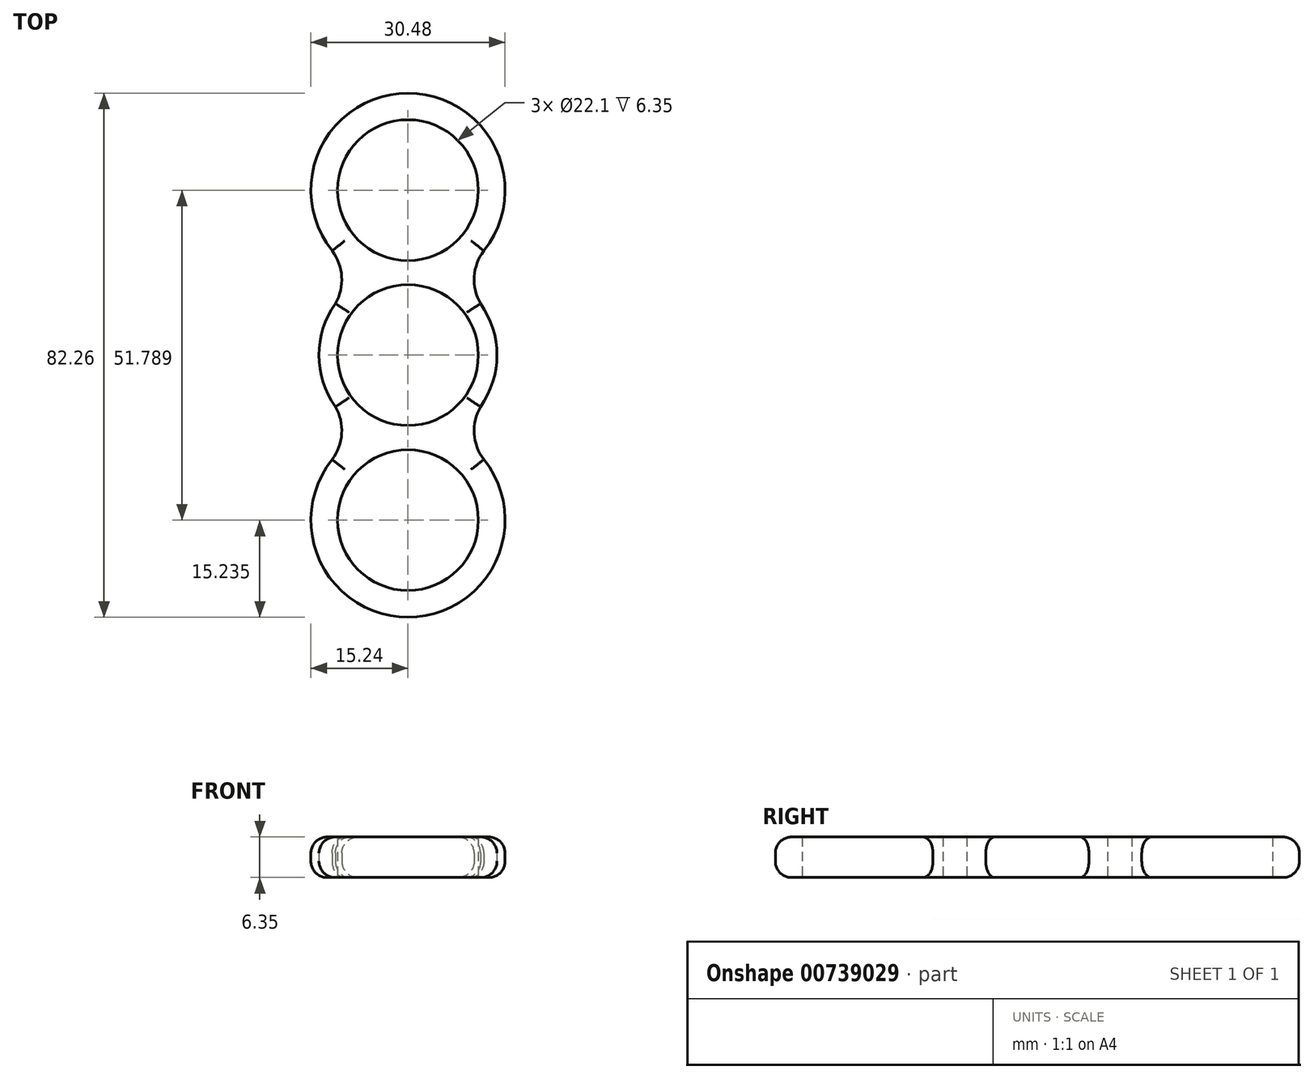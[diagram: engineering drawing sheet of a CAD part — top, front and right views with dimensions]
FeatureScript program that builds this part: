
annotation { "Feature Type Name" : "Feature", "Feature Type Description" : "" }
export const myFeature = defineFeature(function(context is Context, id is Id, definition is map)
    precondition{}
    {
        {
            var Q0;
            Q0=qCreatedBy(makeId("Top.planeOp"),FACE);
            var sketch = newSketch(context, id + "F0", { "sketchPlane" : qUnion([Q0])});
            skArc(sketch, "E0", {"start": v(-11.39, 8.09) * mm, "mid": v(-13.97, 0) * mm, "end": v(-11.39, -8.09) * mm});
            skCircle(sketch, "E1", {"center": v(0, 25.9) * mm, "radius": 11.05 * mm});
            skArc(sketch, "E2", {"start": v(11.9, 16.39) * mm, "mid": v(0, 41.13) * mm, "end": v(-11.9, 16.39) * mm});
            skCircle(sketch, "E3.1.0", {"center": v(0, -25.9) * mm, "radius": 11.05 * mm});
            skArc(sketch, "E3.1.1", {"start": v(-11.9, -16.39) * mm, "mid": v(0, -41.13) * mm, "end": v(11.9, -16.39) * mm});
            skArc(sketch, "E4.trimOffspring", {"start": v(11.39, -8.09) * mm, "mid": v(13.97, 0) * mm, "end": v(11.39, 8.09) * mm});
            skPoint(sketch, "E5.orphan", {"position": v(6.75, 12.23) * mm});
            skArc(sketch, "E6.1.0", {"start": v(11.39, -8.09) * mm, "mid": v(10.4, -12.32) * mm, "end": v(11.9, -16.39) * mm});
            skPoint(sketch, "E7.orphan", {"position": v(-6.75, 12.23) * mm});
            skPoint(sketch, "E8.orphan", {"position": v(-6.75, -12.23) * mm});
            skPoint(sketch, "E9.orphan", {"position": v(6.75, -12.23) * mm});
            skCircle(sketch, "E10", {"center": v(0, 0) * mm, "radius": 11.05 * mm});
            skArc(sketch, "E11", {"start": v(-11.9, -16.39) * mm, "mid": v(-10.4, -12.32) * mm, "end": v(-11.39, -8.09) * mm});
            skArc(sketch, "E12.1.0", {"start": v(-11.39, 8.09) * mm, "mid": v(-10.4, 12.32) * mm, "end": v(-11.9, 16.39) * mm});
            skArc(sketch, "E12.1.1", {"start": v(11.9, 16.39) * mm, "mid": v(10.4, 12.32) * mm, "end": v(11.39, 8.09) * mm});
            skSolve(sketch);
        }
        {
            var Q0;
            Q0 = qSketchRegion(id + "F0", true);
            extrude(context, id + "F1", {"entities" : qUnion([Q0]), "depth" : 6.35 * mm, "offsetDistance" : 25.4 * mm});
        }
        {
            var Q0;
            Q0=makeQuery(id+"F1.opExtrude","CAP_EDGE",EDGE,{"disambiguationData":[OSD([sQuery(id+"F0.wireOp",EDGE,"trfGYVC9-aXAH-ZeNA-1ujl-99YJ1Eel9iI7")])],"isStart":false});
            var Q1;
            Q1=makeQuery(id+"F1.opExtrude","CAP_EDGE",EDGE,{"disambiguationData":[OSD([sQuery(id+"F0.wireOp",EDGE,"E2")])],"isStart":false});
            var Q2;
            Q2=makeQuery(id+"F1.opExtrude","CAP_EDGE",EDGE,{"disambiguationData":[OSD([sQuery(id+"F0.wireOp",EDGE,"s0x0RKGQ-nikB-3b35-0FTQ-KnRF4wtLLO6Y")])],"isStart":false});
            var Q3;
            Q3=makeQuery(id+"F1.opExtrude","CAP_EDGE",EDGE,{"disambiguationData":[OSD([sQuery(id+"F0.wireOp",EDGE,"E4.trimOffspring")])],"isStart":false});
            var Q4;
            Q4=makeQuery(id+"F1.opExtrude","CAP_EDGE",EDGE,{"disambiguationData":[OSD([sQuery(id+"F0.wireOp",EDGE,"E0")])],"isStart":false});
            var Q5;
            Q5=makeQuery(id+"F1.opExtrude","CAP_EDGE",EDGE,{"disambiguationData":[OSD([sQuery(id+"F0.wireOp",EDGE,"2800c864-b789-4809-b79f-413da69f2f8b.1.0")])],"isStart":false});
            var Q6;
            Q6=makeQuery(id+"F1.opExtrude","CAP_EDGE",EDGE,{"disambiguationData":[OSD([sQuery(id+"F0.wireOp",EDGE,"E3.1.1")])],"isStart":false});
            var Q7;
            Q7=makeQuery(id+"F1.opExtrude","CAP_EDGE",EDGE,{"disambiguationData":[OSD([sQuery(id+"F0.wireOp",EDGE,"E6.1.0")])],"isStart":false});
            var Q8;
            Q8=makeQuery(id+"F1.opExtrude","CAP_EDGE",EDGE,{"disambiguationData":[OSD([sQuery(id+"F0.wireOp",EDGE,"E3.1.1")])],"isStart":true});
            var Q9;
            Q9=makeQuery(id+"F1.opExtrude","CAP_EDGE",EDGE,{"disambiguationData":[OSD([sQuery(id+"F0.wireOp",EDGE,"E6.1.0")])],"isStart":true});
            var Q10;
            Q10=makeQuery(id+"F1.opExtrude","CAP_EDGE",EDGE,{"disambiguationData":[OSD([sQuery(id+"F0.wireOp",EDGE,"2800c864-b789-4809-b79f-413da69f2f8b.1.0")])],"isStart":true});
            var Q11;
            Q11=makeQuery(id+"F1.opExtrude","CAP_EDGE",EDGE,{"disambiguationData":[OSD([sQuery(id+"F0.wireOp",EDGE,"E0")])],"isStart":true});
            var Q12;
            Q12=makeQuery(id+"F1.opExtrude","CAP_EDGE",EDGE,{"disambiguationData":[OSD([sQuery(id+"F0.wireOp",EDGE,"E4.trimOffspring")])],"isStart":true});
            var Q13;
            Q13=makeQuery(id+"F1.opExtrude","CAP_EDGE",EDGE,{"disambiguationData":[OSD([sQuery(id+"F0.wireOp",EDGE,"s0x0RKGQ-nikB-3b35-0FTQ-KnRF4wtLLO6Y")])],"isStart":true});
            var Q14;
            Q14=makeQuery(id+"F1.opExtrude","CAP_EDGE",EDGE,{"disambiguationData":[OSD([sQuery(id+"F0.wireOp",EDGE,"trfGYVC9-aXAH-ZeNA-1ujl-99YJ1Eel9iI7")])],"isStart":true});
            var Q15;
            Q15=makeQuery(id+"F1.opExtrude","CAP_EDGE",EDGE,{"disambiguationData":[OSD([sQuery(id+"F0.wireOp",EDGE,"E2")])],"isStart":true});
            fillet(context, id + "F2", {"entities" : qUnion([Q0, Q1, Q2, Q3, Q4, Q5, Q6, Q7, Q8, Q9, Q10, Q11, Q12, Q13, Q14, Q15]), "radius" : 2.54 * mm, "tangentPropagation" : true, "allowEdgeOverflow" : false});
        }
        {
            var Q0;
            Q0 = qSketchRegion(id + "F0", true);
            extrude(context, id + "F3", {"entities" : qUnion([Q0]), "operationType" : NewBodyOperationType.ADD, "depth" : 6.35 * mm, "offsetDistance" : 25.4 * mm});
        }
        {
            var Q0;
            Q0=makeQuery(id+"F3.opExtrude","CAP_EDGE",EDGE,{"disambiguationData":[OSD([sQuery(id+"F0.wireOp",EDGE,"E2")])],"isStart":false});
            var Q1;
            Q1=makeQuery(id+"F3.opExtrude","CAP_EDGE",EDGE,{"disambiguationData":[OSD([sQuery(id+"F0.wireOp",EDGE,"E12.1.0")])],"isStart":false});
            var Q2;
            Q2=makeQuery(id+"F3.opExtrude","CAP_EDGE",EDGE,{"disambiguationData":[OSD([sQuery(id+"F0.wireOp",EDGE,"E0")])],"isStart":false});
            var Q3;
            Q3=makeQuery(id+"F3.opExtrude","CAP_EDGE",EDGE,{"disambiguationData":[OSD([sQuery(id+"F0.wireOp",EDGE,"E3.1.1")])],"isStart":false});
            var Q4;
            Q4=makeQuery(id+"F3.opExtrude","CAP_EDGE",EDGE,{"disambiguationData":[OSD([sQuery(id+"F0.wireOp",EDGE,"E11")])],"isStart":false});
            var Q5;
            Q5=makeQuery(id+"F3.opExtrude","CAP_EDGE",EDGE,{"disambiguationData":[OSD([sQuery(id+"F0.wireOp",EDGE,"E6.1.0")])],"isStart":false});
            var Q6;
            Q6=makeQuery(id+"F3.opExtrude","CAP_EDGE",EDGE,{"disambiguationData":[OSD([sQuery(id+"F0.wireOp",EDGE,"E4.trimOffspring")])],"isStart":false});
            var Q7;
            Q7=makeQuery(id+"F3.opExtrude","CAP_EDGE",EDGE,{"disambiguationData":[OSD([sQuery(id+"F0.wireOp",EDGE,"E12.1.1")])],"isStart":false});
            fillet(context, id + "F4", {"entities" : qUnion([Q0, Q1, Q2, Q3, Q4, Q5, Q6, Q7]), "radius" : 2.54 * mm, "tangentPropagation" : true, "allowEdgeOverflow" : false});
        }
        {
            var Q0;
            Q0=makeQuery(id+"F3.opExtrude","CAP_EDGE",EDGE,{"disambiguationData":[OSD([sQuery(id+"F0.wireOp",EDGE,"E3.1.1")])],"isStart":true});
            var Q1;
            Q1=makeQuery(id+"F3.opExtrude","CAP_EDGE",EDGE,{"disambiguationData":[OSD([sQuery(id+"F0.wireOp",EDGE,"E2")])],"isStart":true});
            var Q2;
            Q2=makeQuery(id+"F3.opExtrude","CAP_EDGE",EDGE,{"disambiguationData":[OSD([sQuery(id+"F0.wireOp",EDGE,"E0")])],"isStart":true});
            var Q3;
            Q3=makeQuery(id+"F3.opExtrude","CAP_EDGE",EDGE,{"disambiguationData":[OSD([sQuery(id+"F0.wireOp",EDGE,"E4.trimOffspring")])],"isStart":true});
            var Q4;
            Q4=makeQuery(id+"F3.opExtrude","CAP_EDGE",EDGE,{"disambiguationData":[OSD([sQuery(id+"F0.wireOp",EDGE,"E12.1.1")])],"isStart":true});
            var Q5;
            Q5=makeQuery(id+"F3.opExtrude","CAP_EDGE",EDGE,{"disambiguationData":[OSD([sQuery(id+"F0.wireOp",EDGE,"E12.1.0")])],"isStart":true});
            var Q6;
            Q6=makeQuery(id+"F3.opExtrude","CAP_EDGE",EDGE,{"disambiguationData":[OSD([sQuery(id+"F0.wireOp",EDGE,"E11")])],"isStart":true});
            var Q7;
            Q7=makeQuery(id+"F3.opExtrude","CAP_EDGE",EDGE,{"disambiguationData":[OSD([sQuery(id+"F0.wireOp",EDGE,"E6.1.0")])],"isStart":true});
            fillet(context, id + "F5", {"entities" : qUnion([Q0, Q1, Q2, Q3, Q4, Q5, Q6, Q7]), "radius" : 2.54 * mm, "tangentPropagation" : true, "allowEdgeOverflow" : false});
        }
    });
